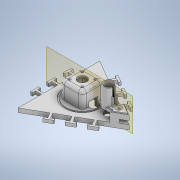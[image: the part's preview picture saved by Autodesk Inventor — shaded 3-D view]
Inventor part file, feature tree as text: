
AUTODESK INVENTOR PART (.ipt)
format: ipt  version: 2022.3 (Build 263350000, 350)  size: 775,168 bytes
history: native  units: mm
features: extrude x29, sketch x24, fillet x7, thicken_offset x6, projected_geometry x5, hole x1, plane x1
ambient origin geometry x8: Origin, YZ Plane, XZ Plane, XY Plane, X Axis, Y Axis, Z Axis, Center Point
bodies: Solid1 (feature_tree)
feature tree (73):
  sketch  "Sketch1"  dims[d1=200.0mm d2=35.0mm]
  extrude  "Extrusion1"  Depth=35.0mm
  extrude  "Extrusion2"  Depth=5.0mm
  sketch  "Sketch2"  dims[d3=5.0mm d4=5.0mm]
  extrude  "Extrusion3"  Depth=40.0mm
  extrude  "Extrusion4"  Depth=40.0mm
  extrude  "Extrusion5"  Depth=10.0mm TaperAngle=0.0deg
  extrude  "Extrusion6"  Depth=42.0mm
  extrude  "Extrusion7"  Depth=6.0mm
  extrude  "Extrusion8"  Depth=10.0mm
  hole  "Hole1"  [1 undecoded]
  fillet  "Fillet1"  Radius=3.0mm
  sketch  "Sketch9"  dims[d43=18.0mm d44=40.0mm d45=0.0mm d46=3.0mm]
  extrude  "Extrusion9"  Depth=10.0mm
  extrude  "Extrusion10"  Depth=80.0mm
  extrude  "Extrusion11"  Depth=2.0mm TaperAngle=0.0deg
  extrude  "Extrusion12"  Depth=22.0mm
  plane  "Work Plane1"
  extrude  "Extrusion13"  Depth=5.0mm
  extrude  "Extrusion14"  Depth=10.0mm
  extrude  "Extrusion15"  TaperAngle=180.0deg  [1 undecoded]
  sketch  "Sketch21"  dims[d56=0.0mm d57=0.0mm d58=22.0mm]
  extrude  "Extrusion18"  Depth=2.0mm
  extrude  "Extrusion19"  Depth=6.0mm
  extrude  "Extrusion20"  Depth=15.0mm TaperAngle=0.0deg
  thicken_offset  "Thicken1"
  fillet  "Fillet7"  Radius=9.0mm
  thicken_offset  "Thicken2"
  thicken_offset  "Thicken3"
  thicken_offset  "Thicken4"
  extrude  "Extrusion21"  Depth=4.0mm
  thicken_offset  "Thicken5"
  extrude  "Extrusion22"  Depth=12.0mm TaperAngle=0.0deg
  fillet  "Fillet8"  Radius=10.0mm
  extrude  "Extrusion23"  Depth=12.0mm
  extrude  "Extrusion24"  Depth=2.0mm
  extrude  "Extrusion25"  Depth=10.0mm TaperAngle=0.0deg
  fillet  "Fillet9"  Radius=45.0mm
  fillet  "Fillet10"  Radius=45.0mm
  extrude  "Extrusion26"  Depth=10.0mm
  extrude  "Extrusion27"  Depth=10.0mm
  extrude  "Extrusion28"  Depth=4.0mm
  extrude  "Extrusion29"  Depth=10.0mm
  fillet  "Fillet11"  Radius=1.388mm
  extrude  "Extrusion31"  Depth=10.0mm
  fillet  "Fillet12"  Radius=1.388mm
  extrude  "Extrusion32"  Depth=8.0mm
  thicken_offset  "Thicken6"
  sketch  "Sketch3"  dims[d5=20.0mm d6=30.0mm d8=40.0mm d9=30.0mm d11=40.0mm]
  sketch  "Sketch4"  dims[d14=30.0mm d16=240.0deg d18=30.0mm d20=40.0mm d21=30.0mm d23=40.0mm]
  sketch  "Sketch5"  dims[d26=30.0mm d28=40.0mm d29=30.0mm d31=40.0mm d34=10.0mm d35=0.0mm]
  sketch  "Sketch6"  dims[d36=2.5mm d37=0.0mm d38=42.0mm]
  projected_geometry  "Projected Loop1"
  sketch  "Sketch7"  dims[d39=42.0mm d40=6.0mm]
  projected_geometry  "Projected Loop2"
  sketch  "Sketch8"  dims[d41=20.0mm d42=10.0mm]
  sketch  "Sketch14"  dims[d47=1.5mm d48=0.0mm d49=10.0mm]
  sketch  "Sketch15"  dims[d50=3.0mm d51=0.0mm d52=80.0mm]
  sketch  "Sketch16"  dims[d53=4.0mm d54=2.0mm d55=0.0mm]
  projected_geometry  "Projected Loop3"
  projected_geometry  "Projected Loop4"
  sketch  "Sketch22"  dims[d59=5.0mm d60=0.0mm d61=31.0mm]
  sketch  "Sketch23"  dims[d62=31.0mm]
  sketch  "Sketch24"  dims[d63=3.2mm d64=6.0mm d65=5.9mm d66=2.0mm d67=90.0deg d68=5.0mm d69=0.0mm d70=10.0mm]
  sketch  "Sketch25"  dims[d72=50.0mm d73=180.0deg]
  sketch  "Sketch26"  dims[d74=22.0mm d75=2.0mm]
  sketch  "Sketch27"  dims[d76=6.0mm d77=6.0mm]
  sketch  "Sketch28"  dims[d78=63.0mm d79=0.0mm d80=15.0mm d81=0.0mm d84=9.0mm d85=0.0mm]
  sketch  "Sketch29"  dims[d86=4.0mm d87=0.0mm d89=0.419mm]
  projected_geometry  "Projected Loop7"
  sketch  "Sketch30"  dims[d95=15.0mm d96=12.0mm d97=12.0mm d98=0.0mm d99=0.0mm d100=10.0mm d101=0.0mm]
  sketch  "Sketch31"  dims[d102=0.0mm d103=0.0mm d119=12.0mm]
  sketch  "Sketch33"  dims[d120=18.0mm d121=2.0mm d122=20.0mm d123=0.0mm d124=45.0mm d125=0.0mm d126=45.0mm d127=0.0mm d128=10.0mm d129=10.0mm d130=4.0mm d131=1.388mm d132=1.388mm d133=1.388mm d134=1.388mm d135=8.0mm d136=8.0mm d137=10.0mm d138=0.0mm d139=9.0mm d140=9.0mm d141=60.0mm d142=18.0mm d143=3.0mm d144=0.0mm d145=2.0mm d146=6.0mm d147=18.0mm d148=0.0mm d149=18.0mm d150=8.0mm d151=0.0mm d152=0.0mm d153=0.0mm d154=0.0mm d155=4.0mm d156=2.0mm d157=4.0mm d160=4.0mm d161=3.0mm d162=4.0mm d165=1.0mm d169=3.0mm d170=4.0mm d171=1.0mm d172=4.0mm d173=20.0mm d174=0.0mm d175=1.5mm d176=2.0mm d177=0.0mm d178=2.0mm d179=18.0mm d180=2.0mm d181=0.0mm d182=16.0mm d183=6.0mm d184=10.0mm d185=0.0mm d188=8.0mm d189=8.2mm d190=20.0mm d191=4.0mm d192=0.0mm d193=2.0mm d194=10.0mm d195=0.0mm d196=0.5mm d197=0.5mm d71=20.594885mm d166=0.872665mm d167=0.5mm d168=0.872665mm]
note: 2 required parameter values undecoded (feature->parameter linkage not recoverable at this tier; creation-order binding heuristic only, values carry confidence <= 0.55)
